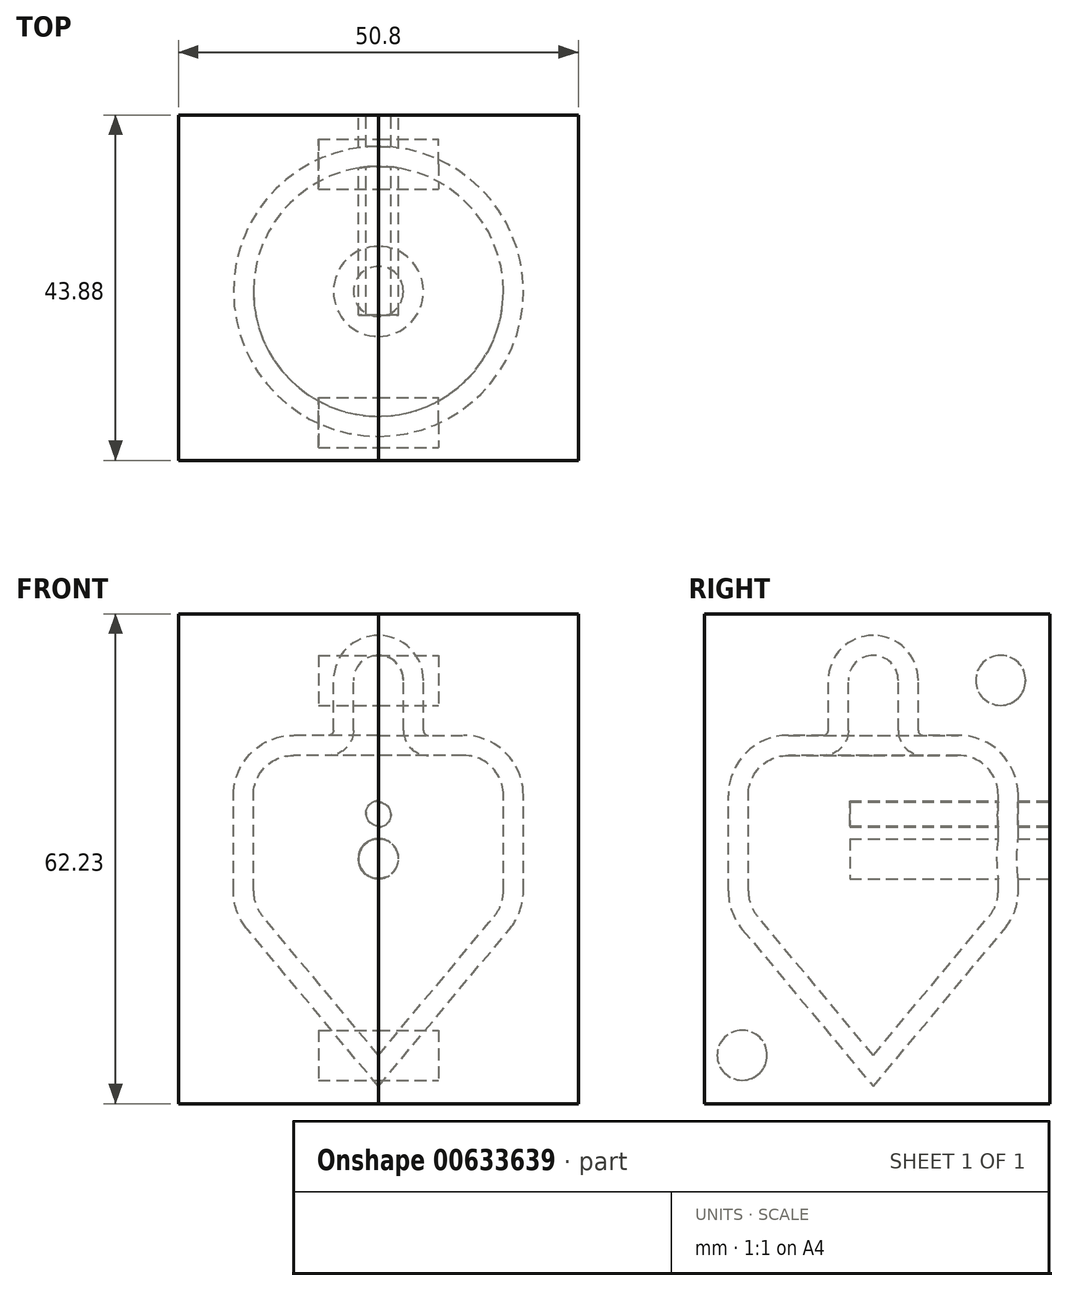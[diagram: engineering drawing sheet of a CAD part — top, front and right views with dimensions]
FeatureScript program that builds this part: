
annotation { "Feature Type Name" : "Feature", "Feature Type Description" : "" }
export const myFeature = defineFeature(function(context is Context, id is Id, definition is map)
    precondition{}
    {
        {
            var Q0;
            Q0=qCreatedBy(makeId("Front.planeOp"),FACE);
            var sketch = newSketch(context, id + "F0", { "sketchPlane" : qUnion([Q0])});
            skLineSegment(sketch, "E0", {"start": v(0, 50.8) * mm, "end": v(0, 0) * mm});
            skLineSegment(sketch, "E1", {"start": v(0, 50.8) * mm, "end": v(3.17, 50.8) * mm});
            skLineSegment(sketch, "E2", {"start": v(3.17, 50.8) * mm, "end": v(3.17, 38.1) * mm});
            skLineSegment(sketch, "E3", {"start": v(3.17, 38.1) * mm, "end": v(15.88, 38.1) * mm});
            skLineSegment(sketch, "E4", {"start": v(15.88, 38.1) * mm, "end": v(15.88, 19.05) * mm});
            skLineSegment(sketch, "E5", {"start": v(15.88, 19.05) * mm, "end": v(0, 0) * mm});
            skSolve(sketch);
        }
        {
            var Q0;
            Q0=makeQuery(id+"F0.imprint","IMPRINT",FACE,{"disambiguationData":[TD([[makeQuery(id+"F0.imprint","IMPRINT",EDGE,{"derivedFrom":sQuery(id+"F0.wireOp",EDGE,"E0")}),1.0]])]});
            var Q1;
            Q1=sQuery(id+"F0.wireOp",EDGE,"E0");
            revolve(context, id + "F1", {"entities" : qUnion([Q0]), "axis" : qUnion([Q1]), "revolveType" : RevolveType.FULL});
        }
        {
            var Q0;
            Q0=makeQuery(id+"F1.opRevolve","SWEPT_FACE",FACE,{"disambiguationData":[OSD([sQuery(id+"F0.wireOp",EDGE,"E2")])]});
            fillet(context, id + "F2", {"entities" : qUnion([Q0]), "radius" : 3.17 * mm, "tangentPropagation" : true, "allowEdgeOverflow" : false});
        }
        {
            var Q0;
            Q0=makeQuery(id+"F1.opRevolve","SWEPT_EDGE",EDGE,{"disambiguationData":[OSD([sQuery(id+"F0.wireOp",EDGE,"E3"),sQuery(id+"F0.wireOp",EDGE,"E4")])]});
            fillet(context, id + "F3", {"entities" : qUnion([Q0]), "radius" : 5.08 * mm, "tangentPropagation" : true, "allowEdgeOverflow" : false});
        }
        {
            var Q0;
            Q0=makeQuery(id+"F1.opRevolve","SWEPT_EDGE",EDGE,{"disambiguationData":[OSD([sQuery(id+"F0.wireOp",EDGE,"E4"),sQuery(id+"F0.wireOp",EDGE,"E5")])]});
            fillet(context, id + "F4", {"entities" : qUnion([Q0]), "radius" : 5.08 * mm, "tangentPropagation" : true, "allowEdgeOverflow" : false});
        }
        {
            var Q0;
            Q0=qCreatedBy(makeId("Top.planeOp"),FACE);
            var sketch = newSketch(context, id + "F5", { "sketchPlane" : qUnion([Q0])});
            skLineSegment(sketch, "E6.bottom", {"start": v(-25.37, 33.7) * mm, "end": v(31.76, 33.7) * mm});
            skLineSegment(sketch, "E6.top", {"start": v(-25.37, -37.26) * mm, "end": v(31.76, -37.26) * mm});
            skLineSegment(sketch, "E6.left", {"start": v(-25.37, 33.7) * mm, "end": v(-25.37, -37.26) * mm});
            skLineSegment(sketch, "E6.right", {"start": v(31.76, 33.7) * mm, "end": v(31.76, -37.26) * mm});
            skSolve(sketch);
        }
        {
            var Q0;
            Q0=makeQuery(id+"F5.imprint","IMPRINT",FACE,{"disambiguationData":[TD([[makeQuery(id+"F5.imprint","IMPRINT",EDGE,{"derivedFrom":sQuery(id+"F5.wireOp",EDGE,"E6.bottom")}),-1.0]])]});
            extrude(context, id + "F6", {"entities" : qUnion([Q0]), "depth" : 31.75 * mm, "offsetDistance" : 25.4 * mm});
        }
        {
            var Q0;
            Q0=makeQuery(id+"F6.opExtrude","SWEPT_BODY",BODY,{"disambiguationData":[OSD([sQuery(id+"F5.wireOp",EDGE,"E6.bottom"),sQuery(id+"F5.wireOp",EDGE,"E6.top"),sQuery(id+"F5.wireOp",EDGE,"E6.left"),sQuery(id+"F5.wireOp",EDGE,"E6.right")])]});
            deleteBodies(context, id + "F7", {"entities" : qUnion([Q0])});
        }
        {
            var Q0;
            Q0=qCreatedBy(makeId("Right.planeOp"),FACE);
            var sketch = newSketch(context, id + "F8", { "sketchPlane" : qUnion([Q0])});
            skLineSegment(sketch, "E7.bottom", {"start": v(-21.46, 56.08) * mm, "end": v(22.42, 56.08) * mm});
            skLineSegment(sketch, "E7.top", {"start": v(-21.46, -6.15) * mm, "end": v(22.42, -6.15) * mm});
            skLineSegment(sketch, "E7.left", {"start": v(-21.46, 56.08) * mm, "end": v(-21.46, -6.15) * mm});
            skLineSegment(sketch, "E7.right", {"start": v(22.42, 56.08) * mm, "end": v(22.42, -6.15) * mm});
            skSolve(sketch);
        }
        {
            var Q0;
            Q0=makeQuery(id+"F8.imprint","IMPRINT",FACE,{"disambiguationData":[TD([[makeQuery(id+"F8.imprint","IMPRINT",EDGE,{"derivedFrom":sQuery(id+"F8.wireOp",EDGE,"E7.bottom")}),-1.0]])]});
            extrude(context, id + "F9", {"entities" : qUnion([Q0]), "depth" : 25.4 * mm, "offsetDistance" : 25.4 * mm});
        }
        {
            var Q0;
            Q0=makeQuery(id+"F1.opRevolve","SWEPT_BODY",BODY,{"disambiguationData":[OSD([sQuery(id+"F0.wireOp",EDGE,"E0"),sQuery(id+"F0.wireOp",EDGE,"E1"),sQuery(id+"F0.wireOp",EDGE,"E2"),sQuery(id+"F0.wireOp",EDGE,"E3"),sQuery(id+"F0.wireOp",EDGE,"E4"),sQuery(id+"F0.wireOp",EDGE,"E5")])]});
            var Q1;
            Q1=makeQuery(id+"F9.opExtrude","SWEPT_BODY",BODY,{"disambiguationData":[OSD([sQuery(id+"F8.wireOp",EDGE,"E7.bottom"),sQuery(id+"F8.wireOp",EDGE,"E7.top"),sQuery(id+"F8.wireOp",EDGE,"E7.left"),sQuery(id+"F8.wireOp",EDGE,"E7.right")])]});
            var Q2;
            Q2=makeQuery(id+"F1.opRevolve","SWEPT_FACE",FACE,{"disambiguationData":[OSD([sQuery(id+"F0.wireOp",EDGE,"E4")])]});
            var Q3;
            Q3=makeQuery(id+"F3.opFillet","BLEND_FACE",FACE,{"disambiguationData":[OSD([sQuery(id+"F0.wireOp",EDGE,"E3"),sQuery(id+"F0.wireOp",EDGE,"E4")])]});
            var Q4;
            Q4=makeQuery(id+"F2.opFillet","BLEND_FACE",FACE,{"disambiguationData":[OSD([sQuery(id+"F0.wireOp",EDGE,"E2"),sQuery(id+"F0.wireOp",EDGE,"E3")])]});
            var Q5;
            Q5=makeQuery(id+"F2.opFillet","BLEND_FACE",FACE,{"disambiguationData":[OSD([sQuery(id+"F0.wireOp",EDGE,"E1"),sQuery(id+"F0.wireOp",EDGE,"E2")])]});
            var Q6;
            Q6=makeQuery(id+"F1.opRevolve","SWEPT_FACE",FACE,{"disambiguationData":[OSD([sQuery(id+"F0.wireOp",EDGE,"E5")])]});
            var Q7;
            Q7=makeQuery(id+"F4.opFillet","BLEND_FACE",FACE,{"disambiguationData":[OSD([sQuery(id+"F0.wireOp",EDGE,"E4"),sQuery(id+"F0.wireOp",EDGE,"E5")])]});
            var Q8;
            Q8=makeQuery(id+"F1.opRevolve","SWEPT_FACE",FACE,{"disambiguationData":[OSD([sQuery(id+"F0.wireOp",EDGE,"E3")])]});
            var Q9;
            Q9=makeQuery(id+"F1.opRevolve","SWEPT_FACE",FACE,{"disambiguationData":[OSD([sQuery(id+"F0.wireOp",EDGE,"E2")])]});
            booleanBodies(context, id + "F10", {"operationType" : BooleanOperationType.SUBTRACTION, "tools" : qUnion([Q0]), "targets" : qUnion([Q1]), "offset" : true, "entitiesToOffset" : qUnion([Q2, Q3, Q4, Q5, Q6, Q7, Q8, Q9]), "offsetDistance" : 2.54 * mm, "keepTools" : true});
        }
        {
            var Q0;
            Q0=makeQuery(id+"F9.opExtrude","SWEPT_BODY",BODY,{"disambiguationData":[OSD([sQuery(id+"F8.wireOp",EDGE,"E7.bottom"),sQuery(id+"F8.wireOp",EDGE,"E7.top"),sQuery(id+"F8.wireOp",EDGE,"E7.left"),sQuery(id+"F8.wireOp",EDGE,"E7.right")])]});
            var Q1;
            Q1=qCreatedBy(makeId("Right.planeOp"),FACE);
            mirror(context, id + "F11", {"entities" : qUnion([Q0]), "mirrorPlane" : qUnion([Q1])});
        }
        {
            var Q0;
            Q0=makeQuery(id+"F11.opPattern","COPY",FACE,{"derivedFrom":makeQuery(id+"F9.opExtrude","CAP_FACE",FACE,{"disambiguationData":[OSD([sQuery(id+"F8.wireOp",EDGE,"E7.bottom"),sQuery(id+"F8.wireOp",EDGE,"E7.top"),sQuery(id+"F8.wireOp",EDGE,"E7.left"),sQuery(id+"F8.wireOp",EDGE,"E7.right")])],"isStart":true}),"instanceName":"1"});
            var sketch = newSketch(context, id + "F12", { "sketchPlane" : qUnion([Q0])});
            skCircle(sketch, "E8", {"center": v(-15.11, 49.99) * mm, "radius": 3.18 * mm});
            skSolve(sketch);
        }
        {
            var Q0;
            Q0=sQuery(id+"F12.wireOp",VERTEX,"E8.center");
            var Q1;
            Q1=makeQuery(id+"F11.opPattern","COPY",BODY,{"derivedFrom":makeQuery(id+"F9.opExtrude","SWEPT_BODY",BODY,{"disambiguationData":[OSD([sQuery(id+"F8.wireOp",EDGE,"E7.bottom"),sQuery(id+"F8.wireOp",EDGE,"E7.top"),sQuery(id+"F8.wireOp",EDGE,"E7.left"),sQuery(id+"F8.wireOp",EDGE,"E7.right")])]}),"instanceName":"1"});
            hole(context, id + "F13", {"style" : HoleStyle.SIMPLE, "endStyle" : HoleEndStyle.BLIND, "holeDiameter" : 6.35 * mm, "majorDiameter" : 6.35 * mm, "holeDepth" : 10.16 * mm, "isTappedThrough" : true, "tappedDepth" : 12.7 * mm, "tapClearance" : 3, "startFromSketch" : true, "locations" : qUnion([Q0]), "scope" : qUnion([Q1])});
        }
        {
            var Q0;
            Q0=makeQuery(id+"F11.opPattern","COPY",BODY,{"derivedFrom":makeQuery(id+"F9.opExtrude","SWEPT_BODY",BODY,{"disambiguationData":[OSD([sQuery(id+"F8.wireOp",EDGE,"E7.bottom"),sQuery(id+"F8.wireOp",EDGE,"E7.top"),sQuery(id+"F8.wireOp",EDGE,"E7.left"),sQuery(id+"F8.wireOp",EDGE,"E7.right")])]}),"instanceName":"1"});
            deleteBodies(context, id + "F14", {"entities" : qUnion([Q0])});
        }
        {
            var Q0;
            Q0=makeQuery(id+"F9.opExtrude","CAP_FACE",FACE,{"disambiguationData":[OSD([sQuery(id+"F8.wireOp",EDGE,"E7.bottom"),sQuery(id+"F8.wireOp",EDGE,"E7.top"),sQuery(id+"F8.wireOp",EDGE,"E7.left"),sQuery(id+"F8.wireOp",EDGE,"E7.right")])],"isStart":true});
            var sketch = newSketch(context, id + "F15", { "sketchPlane" : qUnion([Q0])});
            skCircle(sketch, "E9", {"center": v(-16.18, 47.63) * mm, "radius": 3.18 * mm});
            skPoint(sketch, "E9.centerSnap0", {"position": v(-16.18, 38.4) * mm});
            skSolve(sketch);
        }
        {
            var Q0;
            Q0=makeQuery(id+"F15.imprint","IMPRINT",FACE,{"disambiguationData":[TD([[makeQuery(id+"F15.imprint","IMPRINT",EDGE,{"derivedFrom":sQuery(id+"F15.wireOp",EDGE,"E9")}),1.0]])]});
            extrude(context, id + "F16", {"entities" : qUnion([Q0]), "operationType" : NewBodyOperationType.ADD, "depth" : 7.62 * mm, "offsetDistance" : 25.4 * mm});
        }
        {
            var Q0;
            Q0=makeQuery(id+"F9.opExtrude","CAP_FACE",FACE,{"disambiguationData":[OSD([sQuery(id+"F8.wireOp",EDGE,"E7.bottom"),sQuery(id+"F8.wireOp",EDGE,"E7.top"),sQuery(id+"F8.wireOp",EDGE,"E7.left"),sQuery(id+"F8.wireOp",EDGE,"E7.right")])],"isStart":true});
            var sketch = newSketch(context, id + "F17", { "sketchPlane" : qUnion([Q0])});
            skCircle(sketch, "E10", {"center": v(16.65, 0) * mm, "radius": 3.18 * mm});
            skSolve(sketch);
        }
        {
            var Q0;
            Q0=makeQuery(id+"F17.imprint","IMPRINT",FACE,{"disambiguationData":[TD([[makeQuery(id+"F17.imprint","IMPRINT",EDGE,{"derivedFrom":sQuery(id+"F17.wireOp",EDGE,"E10")}),1.0]])]});
            extrude(context, id + "F18", {"entities" : qUnion([Q0]), "operationType" : NewBodyOperationType.ADD, "depth" : 7.62 * mm, "offsetDistance" : 25.4 * mm});
        }
        {
            var Q0;
            Q0=makeQuery(id+"F9.opExtrude","SWEPT_BODY",BODY,{"disambiguationData":[OSD([sQuery(id+"F8.wireOp",EDGE,"E7.bottom"),sQuery(id+"F8.wireOp",EDGE,"E7.top"),sQuery(id+"F8.wireOp",EDGE,"E7.left"),sQuery(id+"F8.wireOp",EDGE,"E7.right")])]});
            var Q1;
            Q1=qCreatedBy(makeId("Right.planeOp"),FACE);
            mirror(context, id + "F19", {"entities" : qUnion([Q0]), "mirrorPlane" : qUnion([Q1])});
        }
        {
            var Q0;
            Q0=makeQuery(id+"F19.opPattern","COPY",FACE,{"derivedFrom":makeQuery(id+"F16.opExtrude","CAP_FACE",FACE,{"disambiguationData":[OSD([sQuery(id+"F15.wireOp",EDGE,"E9")])],"isStart":false}),"instanceName":"1"});
            extrude(context, id + "F20", {"entities" : qUnion([Q0]), "operationType" : NewBodyOperationType.REMOVE, "oppositeDirection" : true, "depth" : 15.24 * mm, "offsetDistance" : 25.4 * mm});
        }
        {
            var Q0;
            Q0=makeQuery(id+"F19.opPattern","COPY",FACE,{"derivedFrom":makeQuery(id+"F18.opExtrude","CAP_FACE",FACE,{"disambiguationData":[OSD([sQuery(id+"F17.wireOp",EDGE,"E10")])],"isStart":false}),"instanceName":"1"});
            extrude(context, id + "F21", {"entities" : qUnion([Q0]), "operationType" : NewBodyOperationType.REMOVE, "oppositeDirection" : true, "depth" : 15.24 * mm, "offsetDistance" : 25.4 * mm});
        }
        {
            var Q0;
            Q0=makeQuery(id+"F9.opExtrude","SWEPT_FACE",FACE,{"disambiguationData":[OSD([sQuery(id+"F8.wireOp",EDGE,"E7.right")])]});
            var sketch = newSketch(context, id + "F22", { "sketchPlane" : qUnion([Q0])});
            skCircle(sketch, "E11", {"center": v(0, 24.97) * mm, "radius": 2.54 * mm});
            skSolve(sketch);
        }
        {
            var Q0;
            {var subQ0=sQuery(id+"F22.wireOp",EDGE,"E11");var subQ1=makeQuery(id+"F9.opExtrude","CAP_EDGE",EDGE,{"disambiguationData":[OSD([sQuery(id+"F8.wireOp",EDGE,"E7.right")])],"isStart":true});var subQ2=makeQuery(id+"F22.imprint","INTERSECT",VERTEX,{"disambiguationData":[OD(0.0)],"derivedFrom":[subQ1,subQ0]});Q0=makeQuery(id+"F22.imprint","IMPRINT",FACE,{"disambiguationData":[TD([[makeQuery(id+"F22.imprint","IMPRINT",EDGE,{"disambiguationData":[TD([[subQ2,-1.0]])],"derivedFrom":subQ0}),1.0]])]});}
            extrude(context, id + "F23", {"entities" : qUnion([Q0]), "operationType" : NewBodyOperationType.REMOVE, "oppositeDirection" : true, "depth" : 25.4 * mm, "offsetDistance" : 25.4 * mm});
        }
        {
            var Q0;
            Q0=makeQuery(id+"F9.opExtrude","SWEPT_FACE",FACE,{"disambiguationData":[OSD([sQuery(id+"F8.wireOp",EDGE,"E7.right")])]});
            var sketch = newSketch(context, id + "F24", { "sketchPlane" : qUnion([Q0])});
            skCircle(sketch, "E12", {"center": v(0, 30.57) * mm, "radius": 1.59 * mm});
            skSolve(sketch);
        }
        {
            var Q0;
            {var subQ0=sQuery(id+"F24.wireOp",EDGE,"E12");var subQ1=sQuery(id+"F8.wireOp",EDGE,"E7.bottom");var subQ2=sQuery(id+"F8.wireOp",EDGE,"E7.right");var subQ3=makeQuery(id+"F23.boolean.opBoolean","SPLIT",EDGE,{"disambiguationData":[TD([makeQuery(id+"F9.opExtrude","SWEPT_FACE",FACE,{"disambiguationData":[OSD([subQ1])]})])],"derivedFrom":makeQuery(id+"F9.opExtrude","CAP_EDGE",EDGE,{"disambiguationData":[OSD([subQ2])],"isStart":true})});var subQ4=makeQuery(id+"F24.imprint","INTERSECT",VERTEX,{"disambiguationData":[OD(0.0)],"derivedFrom":[subQ3,subQ0]});Q0=makeQuery(id+"F24.imprint","IMPRINT",FACE,{"disambiguationData":[TD([[makeQuery(id+"F24.imprint","IMPRINT",EDGE,{"disambiguationData":[TD([[subQ4,-1.0]])],"derivedFrom":subQ0}),1.0]])]});}
            var Q1;
            Q1=sQuery(id+"F24.wireOp",EDGE,"E12");
            extrude(context, id + "F25", {"entities" : qUnion([Q0]), "operationType" : NewBodyOperationType.REMOVE, "surfaceOperationType" : NewSurfaceOperationType.ADD, "surfaceEntities" : qUnion([Q1]), "oppositeDirection" : true, "depth" : 25.4 * mm, "offsetDistance" : 25.4 * mm});
        }
        {
            var Q0;
            Q0=makeQuery(id+"F19.opPattern","COPY",FACE,{"derivedFrom":makeQuery(id+"F9.opExtrude","SWEPT_FACE",FACE,{"disambiguationData":[OSD([sQuery(id+"F8.wireOp",EDGE,"E7.right")])]}),"instanceName":"1"});
            var sketch = newSketch(context, id + "F26", { "sketchPlane" : qUnion([Q0])});
            skCircle(sketch, "E13", {"center": v(0, 24.97) * mm, "radius": 2.54 * mm});
            skSolve(sketch);
        }
        {
            var Q0;
            {var subQ0=sQuery(id+"F8.wireOp",EDGE,"E7.right");Q0=makeQuery(id+"F26.imprint","IMPRINT",FACE,{"disambiguationData":[TD([[makeQuery(id+"F26.imprint","IMPRINT",EDGE,{"derivedFrom":makeQuery(id+"F19.opPattern","COPY",EDGE,{"derivedFrom":makeQuery(id+"F9.opExtrude","CAP_EDGE",EDGE,{"disambiguationData":[OSD([subQ0])],"isStart":false}),"instanceName":"1"})}),-1.0]])]});}
            var sketch = newSketch(context, id + "F27", { "sketchPlane" : qUnion([Q0])});
            skCircle(sketch, "E14", {"center": v(0, 30.72) * mm, "radius": 1.59 * mm});
            skSolve(sketch);
        }
        {
            var Q0;
            {var subQ0=sQuery(id+"F26.wireOp",EDGE,"E13");var subQ1=makeQuery(id+"F19.opPattern","COPY",EDGE,{"derivedFrom":makeQuery(id+"F9.opExtrude","CAP_EDGE",EDGE,{"disambiguationData":[OSD([sQuery(id+"F8.wireOp",EDGE,"E7.right")])],"isStart":true}),"instanceName":"1"});var subQ2=makeQuery(id+"F26.imprint","INTERSECT",VERTEX,{"disambiguationData":[OD(0.0)],"derivedFrom":[subQ1,subQ0]});Q0=makeQuery(id+"F26.imprint","IMPRINT",FACE,{"disambiguationData":[TD([[makeQuery(id+"F26.imprint","IMPRINT",EDGE,{"disambiguationData":[TD([[subQ2,1.0]])],"derivedFrom":subQ0}),1.0]])]});}
            var Q1;
            Q1=sQuery(id+"F26.wireOp",EDGE,"E13");
            extrude(context, id + "F28", {"entities" : qUnion([Q0]), "operationType" : NewBodyOperationType.REMOVE, "surfaceEntities" : qUnion([Q1]), "oppositeDirection" : true, "depth" : 25.4 * mm, "offsetDistance" : 25.4 * mm});
        }
        {
            var Q0;
            {var subQ0=sQuery(id+"F27.wireOp",EDGE,"E14");var subQ1=sQuery(id+"F8.wireOp",EDGE,"E7.right");var subQ2=makeQuery(id+"F19.opPattern","COPY",EDGE,{"derivedFrom":makeQuery(id+"F9.opExtrude","CAP_EDGE",EDGE,{"disambiguationData":[OSD([subQ1])],"isStart":true}),"instanceName":"1"});var subQ3=makeQuery(id+"F26.imprint","IMPRINT",EDGE,{"disambiguationData":[TD([[makeQuery(id+"F26.imprint","INTERSECT",VERTEX,{"disambiguationData":[OD(0.0)],"derivedFrom":[subQ2,sQuery(id+"F26.wireOp",EDGE,"E13")]}),1.0]])],"derivedFrom":subQ2});var subQ4=makeQuery(id+"F27.imprint","INTERSECT",VERTEX,{"disambiguationData":[OD(0.0)],"derivedFrom":[subQ3,subQ0]});Q0=makeQuery(id+"F27.imprint","IMPRINT",FACE,{"disambiguationData":[TD([[makeQuery(id+"F27.imprint","IMPRINT",EDGE,{"disambiguationData":[TD([[subQ4,1.0]])],"derivedFrom":subQ0}),1.0]])]});}
            extrude(context, id + "F29", {"entities" : qUnion([Q0]), "operationType" : NewBodyOperationType.REMOVE, "oppositeDirection" : true, "depth" : 25.4 * mm, "offsetDistance" : 25.4 * mm});
        }
    });
